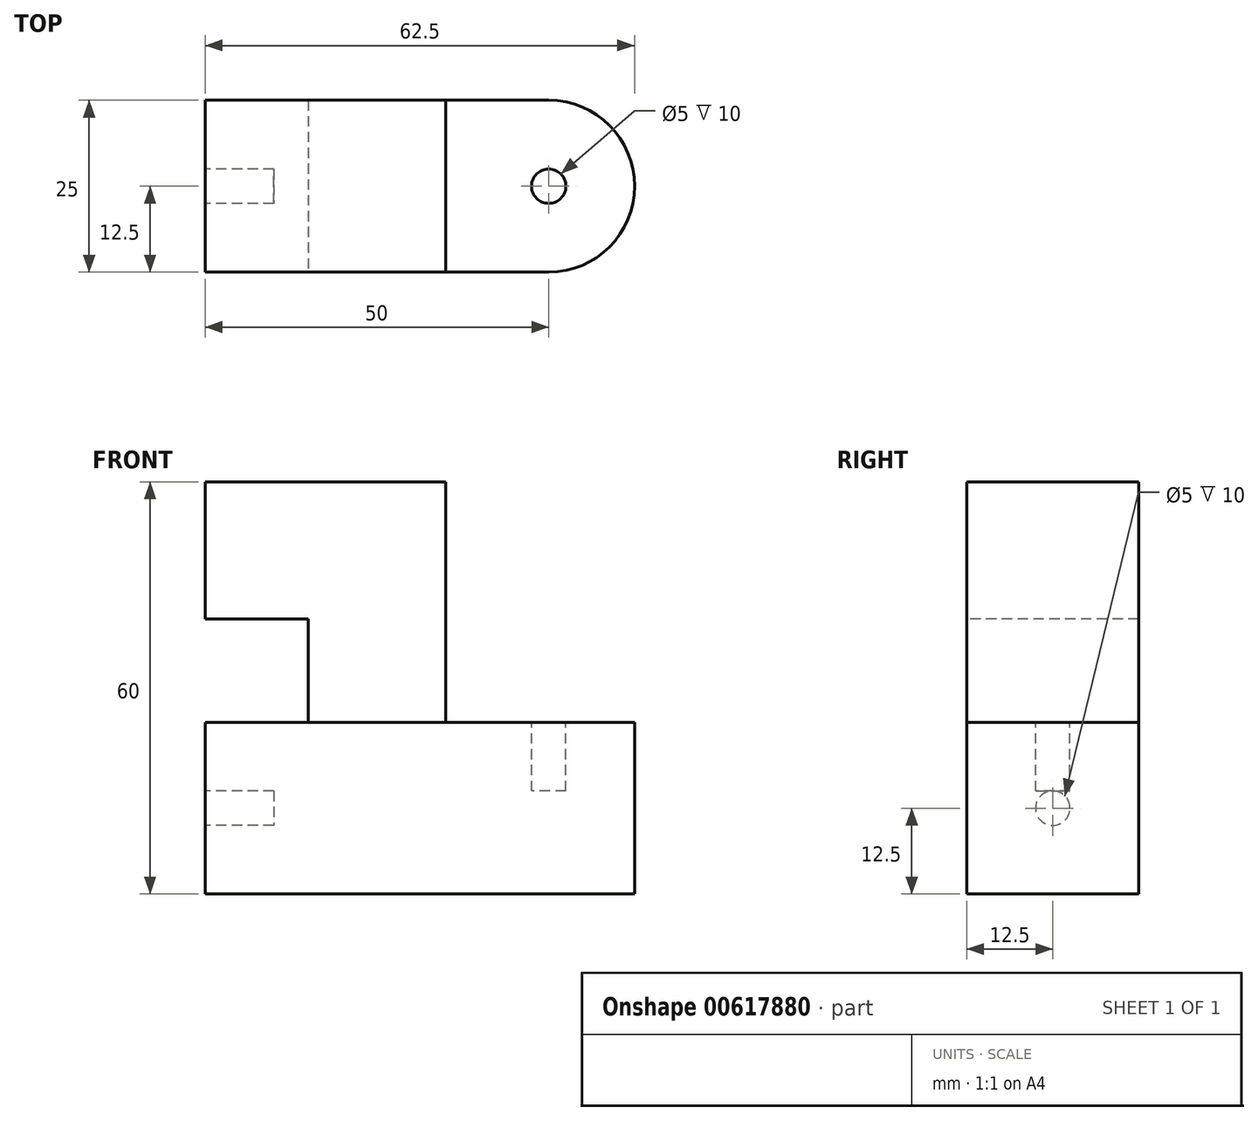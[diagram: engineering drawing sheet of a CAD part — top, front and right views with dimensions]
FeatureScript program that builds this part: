
annotation { "Feature Type Name" : "Feature", "Feature Type Description" : "" }
export const myFeature = defineFeature(function(context is Context, id is Id, definition is map)
    precondition{}
    {
        {
            var Q0;
            Q0=qCreatedBy(makeId("Top.planeOp"),FACE);
            var sketch = newSketch(context, id + "F0", { "sketchPlane" : qUnion([Q0])});
            skLineSegment(sketch, "E0.bottom", {"start": v(25, 12.5) * mm, "end": v(-25, 12.5) * mm});
            skLineSegment(sketch, "E0.top", {"start": v(25, -12.5) * mm, "end": v(-25, -12.5) * mm});
            skLineSegment(sketch, "E0.right", {"start": v(-25, 12.5) * mm, "end": v(-25, -12.5) * mm});
            skPoint(sketch, "E0.middle", {"position": v(0, 0) * mm});
            skArc(sketch, "E1", {"start": v(25, -12.5) * mm, "mid": v(37.5, 0) * mm, "end": v(25, 12.5) * mm});
            skSolve(sketch);
        }
        {
            var Q0;
            Q0=makeQuery(id+"F0.imprint","IMPRINT",FACE,{"disambiguationData":[TD([[makeQuery(id+"F0.imprint","IMPRINT",EDGE,{"derivedFrom":sQuery(id+"F0.wireOp",EDGE,"E0.bottom")}),1.0]])]});
            extrude(context, id + "F1", {"entities" : qUnion([Q0]), "depth" : 25 * mm, "offsetDistance" : 25 * mm});
        }
        {
            var Q0;
            Q0=makeQuery(id+"F1.opExtrude","CAP_FACE",FACE,{"disambiguationData":[OSD([sQuery(id+"F0.wireOp",EDGE,"E0.bottom"),sQuery(id+"F0.wireOp",EDGE,"E0.top"),sQuery(id+"F0.wireOp",EDGE,"E0.right"),sQuery(id+"F0.wireOp",EDGE,"E1")])],"isStart":false});
            var sketch = newSketch(context, id + "F2", { "sketchPlane" : qUnion([Q0])});
            skCircle(sketch, "E2", {"center": v(25, 0) * mm, "radius": 2.5 * mm});
            skSolve(sketch);
        }
        {
            var Q0;
            Q0=makeQuery(id+"F2.imprint","IMPRINT",FACE,{"disambiguationData":[TD([[makeQuery(id+"F2.imprint","IMPRINT",EDGE,{"derivedFrom":sQuery(id+"F2.wireOp",EDGE,"E2")}),1.0]])]});
            extrude(context, id + "F3", {"entities" : qUnion([Q0]), "operationType" : NewBodyOperationType.REMOVE, "oppositeDirection" : true, "depth" : 10 * mm, "offsetDistance" : 25 * mm});
        }
        {
            var Q0;
            Q0=makeQuery(id+"F1.opExtrude","SWEPT_FACE",FACE,{"disambiguationData":[OSD([sQuery(id+"F0.wireOp",EDGE,"E0.right")])]});
            var sketch = newSketch(context, id + "F4", { "sketchPlane" : qUnion([Q0])});
            skLineSegment(sketch, "E3", {"start": v(0, 25) * mm, "end": v(0, 0) * mm, "construction": true});
            skCircle(sketch, "E4", {"center": v(0, 12.5) * mm, "radius": 2.5 * mm});
            skSolve(sketch);
        }
        {
            var Q0;
            Q0=makeQuery(id+"F4.imprint","IMPRINT",FACE,{"disambiguationData":[TD([[makeQuery(id+"F4.imprint","IMPRINT",EDGE,{"derivedFrom":sQuery(id+"F4.wireOp",EDGE,"E4")}),1.0]])]});
            extrude(context, id + "F5", {"entities" : qUnion([Q0]), "operationType" : NewBodyOperationType.REMOVE, "oppositeDirection" : true, "depth" : 10 * mm, "offsetDistance" : 25 * mm});
        }
        {
            var Q0;
            Q0=makeQuery(id+"F1.opExtrude","SWEPT_FACE",FACE,{"disambiguationData":[OSD([sQuery(id+"F0.wireOp",EDGE,"E0.top")])]});
            var sketch = newSketch(context, id + "F6", { "sketchPlane" : qUnion([Q0])});
            skPoint(sketch, "E5.endSnap0", {"position": v(0, 25) * mm});
            skLineSegment(sketch, "E6", {"start": v(-25, 25) * mm, "end": v(-25, 61.15) * mm, "construction": true});
            skLineSegment(sketch, "E7", {"start": v(-10, 25) * mm, "end": v(-10, 40) * mm});
            skLineSegment(sketch, "E8", {"start": v(-10, 40) * mm, "end": v(-25, 40) * mm});
            skLineSegment(sketch, "E9", {"start": v(-25, 40) * mm, "end": v(-25, 60) * mm});
            skLineSegment(sketch, "E10", {"start": v(-25, 60) * mm, "end": v(10, 60) * mm});
            skLineSegment(sketch, "E11", {"start": v(10, 60) * mm, "end": v(10, 25) * mm});
            skSolve(sketch);
        }
        {
            var Q0;
            {var subQ0=sQuery(id+"F6.wireOp",EDGE,"E7");Q0=makeQuery(id+"F6.imprint","IMPRINT",FACE,{"disambiguationData":[TD([[makeQuery(id+"F6.imprint","IMPRINT",EDGE,{"derivedFrom":subQ0}),-1.0]])]});}
            extrude(context, id + "F7", {"entities" : qUnion([Q0]), "oppositeDirection" : true, "depth" : 25 * mm, "offsetDistance" : 25 * mm});
        }
    });
